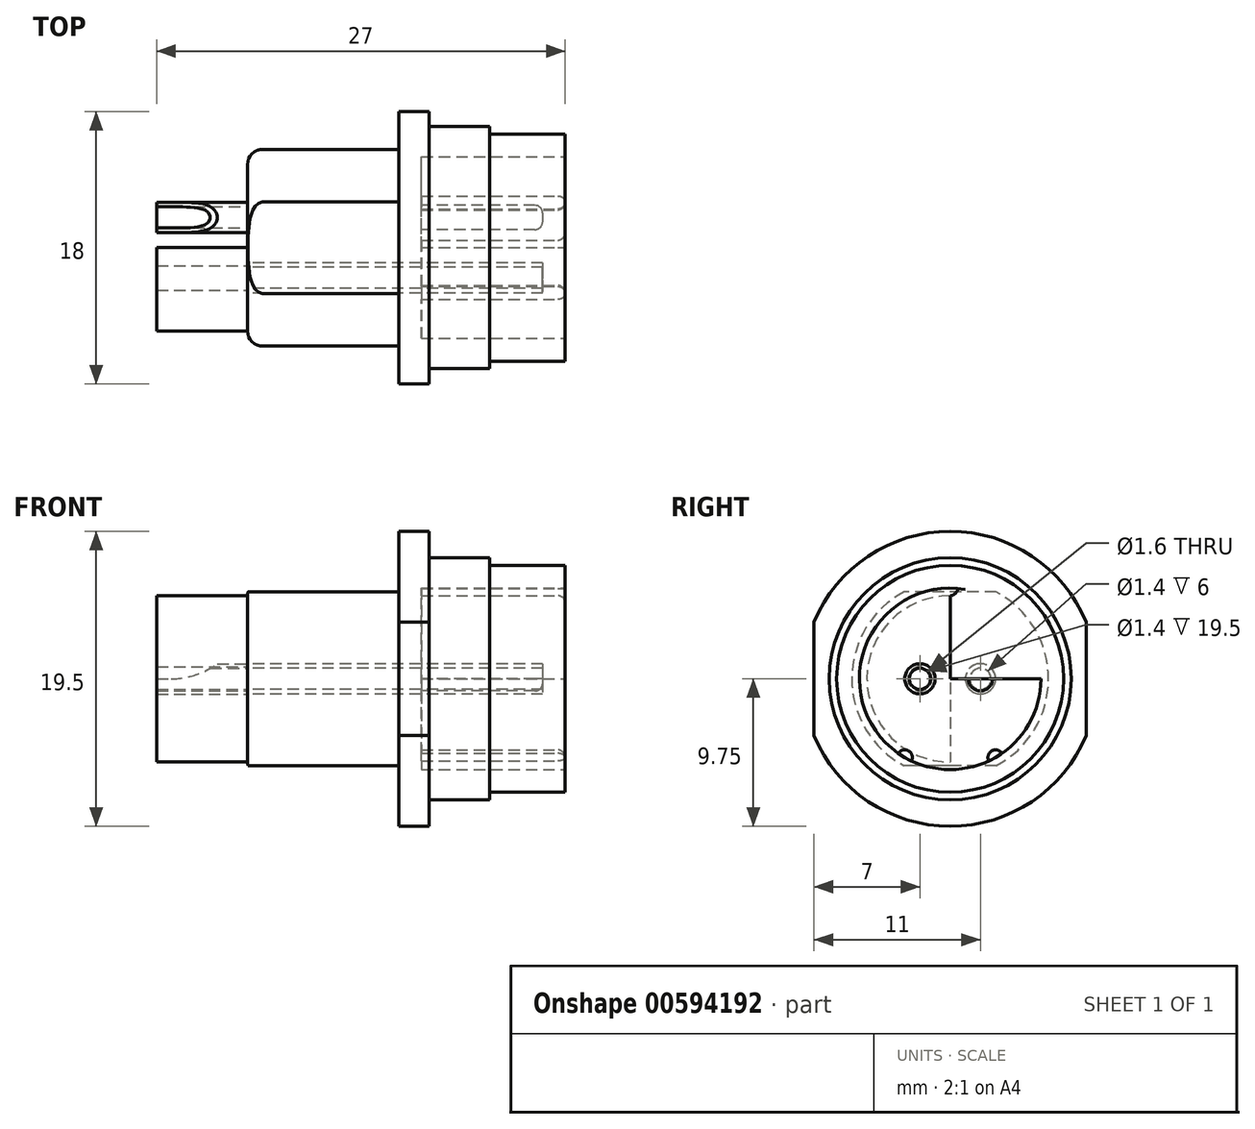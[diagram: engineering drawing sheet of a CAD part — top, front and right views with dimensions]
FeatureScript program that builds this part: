
annotation { "Feature Type Name" : "Feature", "Feature Type Description" : "" }
export const myFeature = defineFeature(function(context is Context, id is Id, definition is map)
    precondition{}
    {
        {
            var Q0;
            Q0=qCreatedBy(makeId("Front.planeOp"),FACE);
            var sketch = newSketch(context, id + "F0", { "sketchPlane" : qUnion([Q0])});
            skLineSegment(sketch, "E0", {"start": v(0, 0) * mm, "end": v(-21, 0) * mm});
            skLineSegment(sketch, "E1", {"start": v(0, 0) * mm, "end": v(0, 8) * mm});
            skLineSegment(sketch, "E2.0", {"start": v(-21, 0) * mm, "end": v(-21, 5.5) * mm});
            skLineSegment(sketch, "E3.0", {"start": v(-11, 6.5) * mm, "end": v(-11, 9.75) * mm});
            skLineSegment(sketch, "E4.0", {"start": v(-9, 8) * mm, "end": v(-9, 9.75) * mm});
            skLineSegment(sketch, "E5.0", {"start": v(-5, 7.5) * mm, "end": v(-5, 8) * mm});
            skLineSegment(sketch, "E6.0", {"start": v(-9, 9.75) * mm, "end": v(-11, 9.75) * mm});
            skLineSegment(sketch, "E7.0", {"start": v(-5, 8) * mm, "end": v(-9, 8) * mm});
            skLineSegment(sketch, "E8.0", {"start": v(0, 7.5) * mm, "end": v(-5, 7.5) * mm});
            skLineSegment(sketch, "E9.trimOffspring", {"start": v(-11, 6.5) * mm, "end": v(-20, 6.5) * mm});
            skPoint(sketch, "E10.visualSharp", {"position": v(-21, 6.5) * mm});
            skArc(sketch, "E10.filletArc", {"start": v(-20, 6.5) * mm, "mid": v(-20.7, 6.2) * mm, "end": v(-21, 5.5) * mm});
            skLineSegment(sketch, "E11.0", {"start": v(0, 6) * mm, "end": v(-9.5, 6) * mm});
            skLineSegment(sketch, "E12.0", {"start": v(-9.5, 0) * mm, "end": v(-9.5, 6) * mm});
            skLineSegment(sketch, "E13.trimOffspring", {"start": v(-20.87, 6) * mm, "end": v(-21, 6) * mm});
            skSolve(sketch);
        }
        {
            var Q0;
            {var subQ2=sQuery(id+"F0.wireOp",EDGE,"E2.0");Q0=makeQuery(id+"F0.imprint","IMPRINT",FACE,{"disambiguationData":[TD([[makeQuery(id+"F0.imprint","IMPRINT",EDGE,{"derivedFrom":subQ2}),-1.0]])]});}
            var Q1;
            Q1=sQuery(id+"F0.wireOp",EDGE,"E0");
            revolve(context, id + "F1", {"entities" : qUnion([Q0]), "axis" : qUnion([Q1]), "revolveType" : RevolveType.FULL});
        }
        {
            var Q0;
            Q0=makeQuery(id+"F1.opRevolve","SWEPT_FACE",FACE,{"disambiguationData":[OSD([sQuery(id+"F0.wireOp",EDGE,"E3.0")])]});
            var sketch = newSketch(context, id + "F2", { "sketchPlane" : qUnion([Q0])});
            skLineSegment(sketch, "E14.0", {"start": v(-9, 15.2) * mm, "end": v(-9, -13.72) * mm});
            skCircle(sketch, "E15.0", {"center": v(0, 0) * mm, "radius": 0.5 * mm});
            skLineSegment(sketch, "E16.0", {"start": v(9, 15.2) * mm, "end": v(9, -13.72) * mm});
            skLineSegment(sketch, "E17.0", {"start": v(-14, 15.2) * mm, "end": v(-14, -13.72) * mm});
            skLineSegment(sketch, "E18.0", {"start": v(14, 15.2) * mm, "end": v(14, -13.72) * mm});
            skLineSegment(sketch, "E19", {"start": v(-14, 15.2) * mm, "end": v(-9, 15.2) * mm});
            skLineSegment(sketch, "E20", {"start": v(9, 15.2) * mm, "end": v(14, 15.2) * mm});
            skLineSegment(sketch, "E21", {"start": v(-14, -13.72) * mm, "end": v(-9, -13.72) * mm});
            skLineSegment(sketch, "E22", {"start": v(9, -13.72) * mm, "end": v(14, -13.72) * mm});
            skSolve(sketch);
        }
        {
            var Q0;
            {var subQ0=sQuery(id+"F2.wireOp",EDGE,"E16.0");var subQ1=makeQuery(id+"F1.opRevolve","SWEPT_EDGE",EDGE,{"disambiguationData":[OSD([sQuery(id+"F0.wireOp",EDGE,"E3.0"),sQuery(id+"F0.wireOp",EDGE,"E6.0")])]});var subQ2=makeQuery(id+"F2.imprint","INTERSECT",VERTEX,{"disambiguationData":[OD(0.0)],"derivedFrom":[subQ1,subQ0]});Q0=makeQuery(id+"F2.imprint","IMPRINT",FACE,{"disambiguationData":[TD([[makeQuery(id+"F2.imprint","IMPRINT",EDGE,{"disambiguationData":[TD([[subQ2,-1.0]])],"derivedFrom":subQ0}),1.0]])]});}
            var Q1;
            Q1=makeQuery(id+"F2.imprint","IMPRINT",FACE,{"disambiguationData":[TD([[makeQuery(id+"F2.imprint","IMPRINT",EDGE,{"derivedFrom":sQuery(id+"F2.wireOp",EDGE,"E18.0")}),-1.0]])]});
            var Q2;
            {var subQ0=sQuery(id+"F2.wireOp",EDGE,"E14.0");var subQ1=makeQuery(id+"F1.opRevolve","SWEPT_EDGE",EDGE,{"disambiguationData":[OSD([sQuery(id+"F0.wireOp",EDGE,"E3.0"),sQuery(id+"F0.wireOp",EDGE,"E6.0")])]});var subQ2=makeQuery(id+"F2.imprint","INTERSECT",VERTEX,{"disambiguationData":[OD(0.0)],"derivedFrom":[subQ1,subQ0]});Q2=makeQuery(id+"F2.imprint","IMPRINT",FACE,{"disambiguationData":[TD([[makeQuery(id+"F2.imprint","IMPRINT",EDGE,{"disambiguationData":[TD([[subQ2,-1.0]])],"derivedFrom":subQ0}),-1.0]])]});}
            var Q3;
            Q3=makeQuery(id+"F2.imprint","IMPRINT",FACE,{"disambiguationData":[TD([[makeQuery(id+"F2.imprint","IMPRINT",EDGE,{"derivedFrom":sQuery(id+"F2.wireOp",EDGE,"E17.0")}),1.0]])]});
            extrude(context, id + "F3", {"entities" : qUnion([Q0, Q1, Q2, Q3]), "operationType" : NewBodyOperationType.REMOVE, "depth" : 25 * mm, "offsetDistance" : 25 * mm, "symmetric" : true});
        }
        {
            var Q0;
            Q0=makeQuery(id+"F1.opRevolve","SWEPT_FACE",FACE,{"disambiguationData":[OSD([sQuery(id+"F0.wireOp",EDGE,"E2.0")])]});
            var sketch = newSketch(context, id + "F4", { "sketchPlane" : qUnion([Q0])});
            skLineSegment(sketch, "E23", {"start": v(-11.68, 0) * mm, "end": v(11.55, 0) * mm});
            skLineSegment(sketch, "E24.0", {"start": v(-11.68, -5.75) * mm, "end": v(11.55, -5.75) * mm});
            skLineSegment(sketch, "E25.0", {"start": v(-11.68, 5.75) * mm, "end": v(11.55, 5.75) * mm});
            skLineSegment(sketch, "E26.0", {"start": v(-11.68, 10.75) * mm, "end": v(11.55, 10.75) * mm});
            skLineSegment(sketch, "E27.0", {"start": v(-11.68, -10.75) * mm, "end": v(11.55, -10.75) * mm});
            skLineSegment(sketch, "E28", {"start": v(-11.68, 10.75) * mm, "end": v(-11.68, 5.75) * mm});
            skLineSegment(sketch, "E29", {"start": v(11.55, -10.75) * mm, "end": v(11.55, -5.75) * mm});
            skLineSegment(sketch, "E30", {"start": v(-11.68, -10.75) * mm, "end": v(-11.68, -5.75) * mm});
            skLineSegment(sketch, "E31", {"start": v(11.55, 10.75) * mm, "end": v(11.55, 5.75) * mm});
            skSolve(sketch);
        }
        {
            var Q0;
            Q0=makeQuery(id+"F4.imprint","IMPRINT",FACE,{"disambiguationData":[TD([[makeQuery(id+"F4.imprint","IMPRINT",EDGE,{"derivedFrom":sQuery(id+"F4.wireOp",EDGE,"E25.0")}),1.0]])]});
            var Q1;
            Q1=makeQuery(id+"F4.imprint","IMPRINT",FACE,{"disambiguationData":[TD([[makeQuery(id+"F4.imprint","IMPRINT",EDGE,{"derivedFrom":sQuery(id+"F4.wireOp",EDGE,"E24.0")}),-1.0]])]});
            extrude(context, id + "F5", {"entities" : qUnion([Q0, Q1]), "operationType" : NewBodyOperationType.REMOVE, "oppositeDirection" : true, "depth" : 10 * mm, "offsetDistance" : 25 * mm});
        }
        {
            var Q0;
            Q0=makeQuery(id+"F1.opRevolve","SWEPT_FACE",FACE,{"disambiguationData":[OSD([sQuery(id+"F0.wireOp",EDGE,"E2.0")])]});
            var sketch = newSketch(context, id + "F6", { "sketchPlane" : qUnion([Q0])});
            skLineSegment(sketch, "E32", {"start": v(0, 12.25) * mm, "end": v(0, -11.9) * mm});
            skCircle(sketch, "E33", {"center": v(-2, 0) * mm, "radius": 1 * mm});
            skCircle(sketch, "E34", {"center": v(-2, 0) * mm, "radius": 0.7 * mm});
            skCircle(sketch, "E35", {"center": v(-2, 0) * mm, "radius": 0.8 * mm});
            skPoint(sketch, "E36.orphan", {"position": v(-12.53, 0) * mm});
            skCircle(sketch, "E37.MirrorC", {"center": v(2, 0) * mm, "radius": 1 * mm});
            skCircle(sketch, "E38.MirrorC", {"center": v(2, 0) * mm, "radius": 0.8 * mm});
            skCircle(sketch, "E39.MirrorC", {"center": v(2, 0) * mm, "radius": 0.7 * mm});
            skSolve(sketch);
        }
        {
            var Q0;
            Q0=makeQuery(id+"F6.imprint","IMPRINT",FACE,{"disambiguationData":[TD([[makeQuery(id+"F6.imprint","IMPRINT",EDGE,{"derivedFrom":sQuery(id+"F6.wireOp",EDGE,"E34")}),-1.0]])]});
            var Q1;
            Q1=makeQuery(id+"F6.imprint","IMPRINT",FACE,{"disambiguationData":[TD([[makeQuery(id+"F6.imprint","IMPRINT",EDGE,{"derivedFrom":sQuery(id+"F6.wireOp",EDGE,"E34")}),1.0]])]});
            var Q2;
            Q2=makeQuery(id+"F6.imprint","IMPRINT",FACE,{"disambiguationData":[TD([[makeQuery(id+"F6.imprint","IMPRINT",EDGE,{"derivedFrom":sQuery(id+"F6.wireOp",EDGE,"E39.MirrorC")}),-1.0]])]});
            var Q3;
            Q3=makeQuery(id+"F6.imprint","IMPRINT",FACE,{"disambiguationData":[TD([[makeQuery(id+"F6.imprint","IMPRINT",EDGE,{"derivedFrom":sQuery(id+"F6.wireOp",EDGE,"E38.MirrorC")}),-1.0]])]});
            extrude(context, id + "F7", {"entities" : qUnion([Q0, Q1, Q2, Q3]), "oppositeDirection" : true, "depth" : 19.5 * mm, "offsetDistance" : 25 * mm});
        }
        {
            var Q0;
            Q0=makeQuery(id+"F7.opExtrude","CAP_FACE",FACE,{"disambiguationData":[OSD([sQuery(id+"F6.wireOp",EDGE,"E38.MirrorC")])],"isStart":false});
            var Q1;
            Q1=makeQuery(id+"F7.opExtrude","CAP_EDGE",EDGE,{"disambiguationData":[OSD([sQuery(id+"F6.wireOp",EDGE,"E35")])],"isStart":false});
            fillet(context, id + "F8", {"entities" : qUnion([Q0, Q1]), "radius" : 0.5 * mm, "tangentPropagation" : true, "allowEdgeOverflow" : false});
        }
        {
            var Q0;
            Q0=makeQuery(id+"F6.imprint","IMPRINT",FACE,{"disambiguationData":[TD([[makeQuery(id+"F6.imprint","IMPRINT",EDGE,{"derivedFrom":sQuery(id+"F6.wireOp",EDGE,"E38.MirrorC")}),-1.0]])]});
            var Q1;
            Q1=makeQuery(id+"F6.imprint","IMPRINT",FACE,{"disambiguationData":[TD([[makeQuery(id+"F6.imprint","IMPRINT",EDGE,{"derivedFrom":sQuery(id+"F6.wireOp",EDGE,"E37.MirrorC")}),-1.0]])]});
            var Q2;
            Q2=makeQuery(id+"F6.imprint","IMPRINT",FACE,{"disambiguationData":[TD([[makeQuery(id+"F6.imprint","IMPRINT",EDGE,{"derivedFrom":sQuery(id+"F6.wireOp",EDGE,"E34")}),-1.0]])]});
            var Q3;
            Q3=makeQuery(id+"F6.imprint","IMPRINT",FACE,{"disambiguationData":[TD([[makeQuery(id+"F6.imprint","IMPRINT",EDGE,{"derivedFrom":sQuery(id+"F6.wireOp",EDGE,"E33")}),1.0]])]});
            extrude(context, id + "F9", {"entities" : qUnion([Q0, Q1, Q2, Q3]), "depth" : 6 * mm, "offsetDistance" : 25 * mm});
        }
        {
            var Q0;
            Q0=makeQuery(id+"F3.boolean.opBoolean","COPY",FACE,{"derivedFrom":makeQuery(id+"F3.opExtrude","SWEPT_FACE",FACE,{"disambiguationData":[OSD([sQuery(id+"F2.wireOp",EDGE,"E16.0")])]})});
            var sketch = newSketch(context, id + "F10", { "sketchPlane" : qUnion([Q0])});
            skLineSegment(sketch, "E40", {"start": v(0.65, 0) * mm, "end": v(-9, 0) * mm});
            skPoint(sketch, "E40.endSnap0", {"position": v(-9, 0) * mm});
            skLineSegment(sketch, "E41", {"start": v(-9, 0) * mm, "end": v(-9, 5.8) * mm});
            skLineSegment(sketch, "E42.0", {"start": v(-29, 0) * mm, "end": v(-29, 5) * mm});
            skLineSegment(sketch, "E43.0", {"start": v(-23, 1) * mm, "end": v(-23, 5) * mm});
            skArc(sketch, "E44", {"start": v(-26.06, 0) * mm, "mid": v(-24.45, 0.26) * mm, "end": v(-23, 1) * mm});
            skLineSegment(sketch, "E45.0", {"start": v(0.65, 5) * mm, "end": v(-9, 5) * mm});
            skLineSegment(sketch, "E46.trimOffspring", {"start": v(-23, 5) * mm, "end": v(-29, 5) * mm});
            skLineSegment(sketch, "E47.trimOffspring", {"start": v(-26.06, 0) * mm, "end": v(-29, 0) * mm});
            skPoint(sketch, "E48.orphan", {"position": v(-41.52, 0) * mm});
            skSolve(sketch);
        }
        {
            var Q0;
            Q0=makeQuery(id+"F10.imprint","IMPRINT",FACE,{"disambiguationData":[TD([[makeQuery(id+"F10.imprint","IMPRINT",EDGE,{"derivedFrom":sQuery(id+"F10.wireOp",EDGE,"E42.0")}),-1.0]])]});
            extrude(context, id + "F11", {"entities" : qUnion([Q0]), "oppositeDirection" : true, "depth" : 25 * mm, "offsetDistance" : 25 * mm});
        }
        {
            var Q0;
            Q0=makeQuery(id+"F11.opExtrude","SWEPT_BODY",BODY,{"disambiguationData":[OSD([sQuery(id+"F10.wireOp",EDGE,"E42.0"),sQuery(id+"F10.wireOp",EDGE,"E43.0"),sQuery(id+"F10.wireOp",EDGE,"E44"),sQuery(id+"F10.wireOp",EDGE,"E46.trimOffspring"),sQuery(id+"F10.wireOp",EDGE,"E47.trimOffspring")])]});
            var Q1;
            Q1=makeQuery(id+"F9.opExtrude","SWEPT_BODY",BODY,{"disambiguationData":[OSD([sQuery(id+"F6.wireOp",EDGE,"E33"),sQuery(id+"F6.wireOp",EDGE,"E34")])]});
            var Q2;
            Q2=makeQuery(id+"F9.opExtrude","SWEPT_BODY",BODY,{"disambiguationData":[OSD([sQuery(id+"F6.wireOp",EDGE,"E37.MirrorC"),sQuery(id+"F6.wireOp",EDGE,"E39.MirrorC")])]});
            booleanBodies(context, id + "F12", {"operationType" : BooleanOperationType.SUBTRACTION, "tools" : qUnion([Q0]), "targets" : qUnion([Q1, Q2])});
        }
        {
            var Q0;
            Q0=makeQuery(id+"F1.opRevolve","SWEPT_FACE",FACE,{"disambiguationData":[OSD([sQuery(id+"F0.wireOp",EDGE,"E1")])]});
            var sketch = newSketch(context, id + "F13", { "sketchPlane" : qUnion([Q0])});
            skLineSegment(sketch, "E49", {"start": v(-11.1, 0) * mm, "end": v(11.26, 0) * mm});
            skCircle(sketch, "E50", {"center": v(0, 0) * mm, "radius": 6 * mm});
            skLineSegment(sketch, "E51", {"start": v(0, 0) * mm, "end": v(0, 5.5) * mm});
            skLineSegment(sketch, "E52", {"start": v(0, 0) * mm, "end": v(-2.75, -4.76) * mm});
            skLineSegment(sketch, "E53.MirrorCS", {"start": v(0, 0) * mm, "end": v(2.75, -4.76) * mm});
            skArc(sketch, "E54", {"start": v(-0.5, 5.98) * mm, "mid": v(0, 5.5) * mm, "end": v(0.5, 5.98) * mm});
            skArc(sketch, "E55", {"start": v(-2.56, -5.43) * mm, "mid": v(-2.75, -4.76) * mm, "end": v(-3.42, -4.93) * mm});
            skArc(sketch, "E56", {"start": v(3.42, -4.93) * mm, "mid": v(2.75, -4.76) * mm, "end": v(2.56, -5.43) * mm});
            skSolve(sketch);
        }
        {
            var Q0;
            {var subQ0=sQuery(id+"F13.wireOp",EDGE,"E56");var subQ1=sQuery(id+"F13.wireOp",EDGE,"E50");var subQ2=makeQuery(id+"F13.imprint","INTERSECT",VERTEX,{"disambiguationData":[OD(0.0)],"derivedFrom":[subQ1,subQ0]});Q0=makeQuery(id+"F13.imprint","IMPRINT",FACE,{"disambiguationData":[TD([[makeQuery(id+"F13.imprint","IMPRINT",EDGE,{"disambiguationData":[TD([[subQ2,1.0]])],"derivedFrom":subQ1}),1.0]])]});}
            var Q1;
            {var subQ0=sQuery(id+"F13.wireOp",EDGE,"E55");var subQ1=sQuery(id+"F13.wireOp",EDGE,"E50");var subQ2=makeQuery(id+"F13.imprint","INTERSECT",VERTEX,{"disambiguationData":[OD(0.0)],"derivedFrom":[subQ1,subQ0]});Q1=makeQuery(id+"F13.imprint","IMPRINT",FACE,{"disambiguationData":[TD([[makeQuery(id+"F13.imprint","IMPRINT",EDGE,{"disambiguationData":[TD([[subQ2,1.0]])],"derivedFrom":subQ1}),1.0]])]});}
            var Q2;
            {var subQ0=sQuery(id+"F13.wireOp",EDGE,"E54");var subQ1=sQuery(id+"F13.wireOp",EDGE,"E50");var subQ2=makeQuery(id+"F13.imprint","INTERSECT",VERTEX,{"disambiguationData":[OD(0.0)],"derivedFrom":[subQ1,subQ0]});Q2=makeQuery(id+"F13.imprint","IMPRINT",FACE,{"disambiguationData":[TD([[makeQuery(id+"F13.imprint","IMPRINT",EDGE,{"disambiguationData":[TD([[subQ2,1.0]])],"derivedFrom":subQ1}),1.0]])]});}
            extrude(context, id + "F14", {"entities" : qUnion([Q0, Q1, Q2]), "operationType" : NewBodyOperationType.ADD, "oppositeDirection" : true, "depth" : 10 * mm, "offsetDistance" : 25 * mm});
        }
        {
            var Q0;
            Q0=makeQuery(id+"F14.opExtrude","CAP_EDGE",EDGE,{"disambiguationData":[OSD([sQuery(id+"F13.wireOp",EDGE,"E56")])],"isStart":true});
            var Q1;
            Q1=makeQuery(id+"F14.opExtrude","CAP_EDGE",EDGE,{"disambiguationData":[OSD([sQuery(id+"F13.wireOp",EDGE,"E55")])],"isStart":true});
            var Q2;
            Q2=makeQuery(id+"F14.opExtrude","CAP_EDGE",EDGE,{"disambiguationData":[OSD([sQuery(id+"F13.wireOp",EDGE,"E54")])],"isStart":true});
            fillet(context, id + "F15", {"entities" : qUnion([Q0, Q1, Q2]), "radius" : 0.5 * mm, "tangentPropagation" : true, "allowEdgeOverflow" : false});
        }
    });
